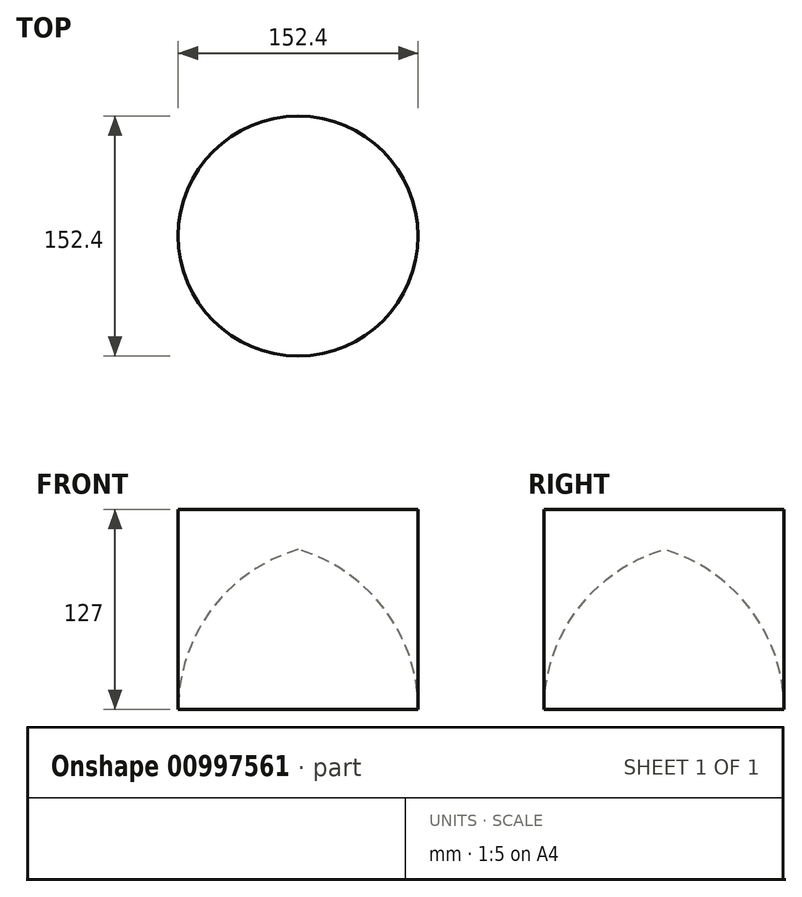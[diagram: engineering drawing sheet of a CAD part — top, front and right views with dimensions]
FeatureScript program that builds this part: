
annotation { "Feature Type Name" : "Feature", "Feature Type Description" : "" }
export const myFeature = defineFeature(function(context is Context, id is Id, definition is map)
    precondition{}
    {
        {
            var Q0;
            Q0=qCreatedBy(makeId("Front.planeOp"),FACE);
            var sketch = newSketch(context, id + "F0", { "sketchPlane" : qUnion([Q0])});
            skLineSegment(sketch, "E0", {"start": v(0, 25.4) * mm, "end": v(0, 0) * mm});
            skLineSegment(sketch, "E1", {"start": v(0, 25.4) * mm, "end": v(-76.2, 25.4) * mm});
            skLineSegment(sketch, "E2", {"start": v(-76.2, 25.4) * mm, "end": v(-76.2, -101.6) * mm});
            skArc(sketch, "E3", {"start": v(0, 0) * mm, "mid": v(-55.03, -38.1) * mm, "end": v(-76.2, -101.6) * mm});
            skLineSegment(sketch, "E4", {"start": v(-76.2, -101.6) * mm, "end": v(0, -101.6) * mm, "construction": true});
            skLineSegment(sketch, "E5", {"start": v(0, -101.6) * mm, "end": v(0, 0) * mm, "construction": true});
            skSolve(sketch);
        }
        {
            var Q0;
            Q0=makeQuery(id+"F0.imprint","IMPRINT",FACE,{"disambiguationData":[TD([[makeQuery(id+"F0.imprint","IMPRINT",EDGE,{"derivedFrom":sQuery(id+"F0.wireOp",EDGE,"E0")}),-1.0]])]});
            var Q1;
            Q1=sQuery(id+"F0.wireOp",EDGE,"E0");
            revolve(context, id + "F1", {"surfaceOperationType" : NewSurfaceOperationType.NEW, "entities" : qUnion([Q0]), "axis" : qUnion([Q1]), "revolveType" : RevolveType.FULL});
        }
    });
